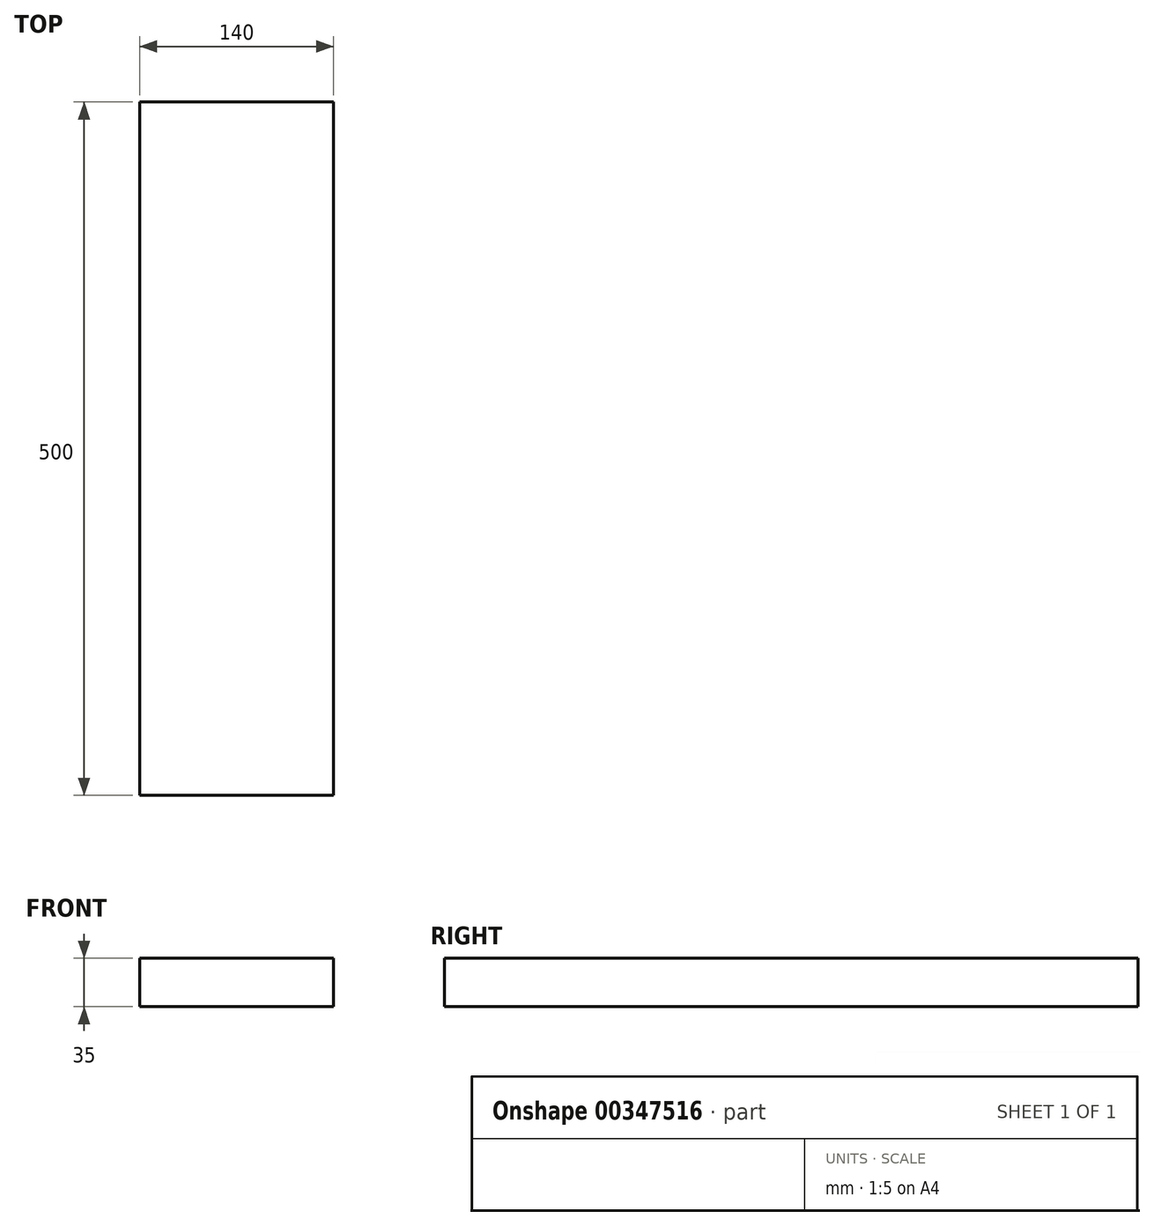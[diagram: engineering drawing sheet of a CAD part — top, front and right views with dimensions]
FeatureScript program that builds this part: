
annotation { "Feature Type Name" : "Feature", "Feature Type Description" : "" }
export const myFeature = defineFeature(function(context is Context, id is Id, definition is map)
    precondition{}
    {
        {
            var Q0;
            Q0=qCreatedBy(makeId("Front.planeOp"),FACE);
            var sketch = newSketch(context, id + "F0", { "sketchPlane" : qUnion([Q0])});
            skLineSegment(sketch, "E0.bottom", {"start": v(-70, 0) * mm, "end": v(70, 0) * mm});
            skLineSegment(sketch, "E0.top", {"start": v(-70, -35) * mm, "end": v(70, -35) * mm});
            skLineSegment(sketch, "E0.left", {"start": v(-70, 0) * mm, "end": v(-70, -35) * mm});
            skLineSegment(sketch, "E0.right", {"start": v(70, 0) * mm, "end": v(70, -35) * mm});
            skSolve(sketch);
        }
        {
            var Q0;
            Q0=makeQuery(id+"F0.imprint","IMPRINT",FACE,{"disambiguationData":[TD([[makeQuery(id+"F0.imprint","IMPRINT",EDGE,{"derivedFrom":sQuery(id+"F0.wireOp",EDGE,"E0.bottom")}),-1.0]])]});
            extrude(context, id + "F1", {"entities" : qUnion([Q0]), "oppositeDirection" : true, "depth" : 500 * mm});
        }
    });
